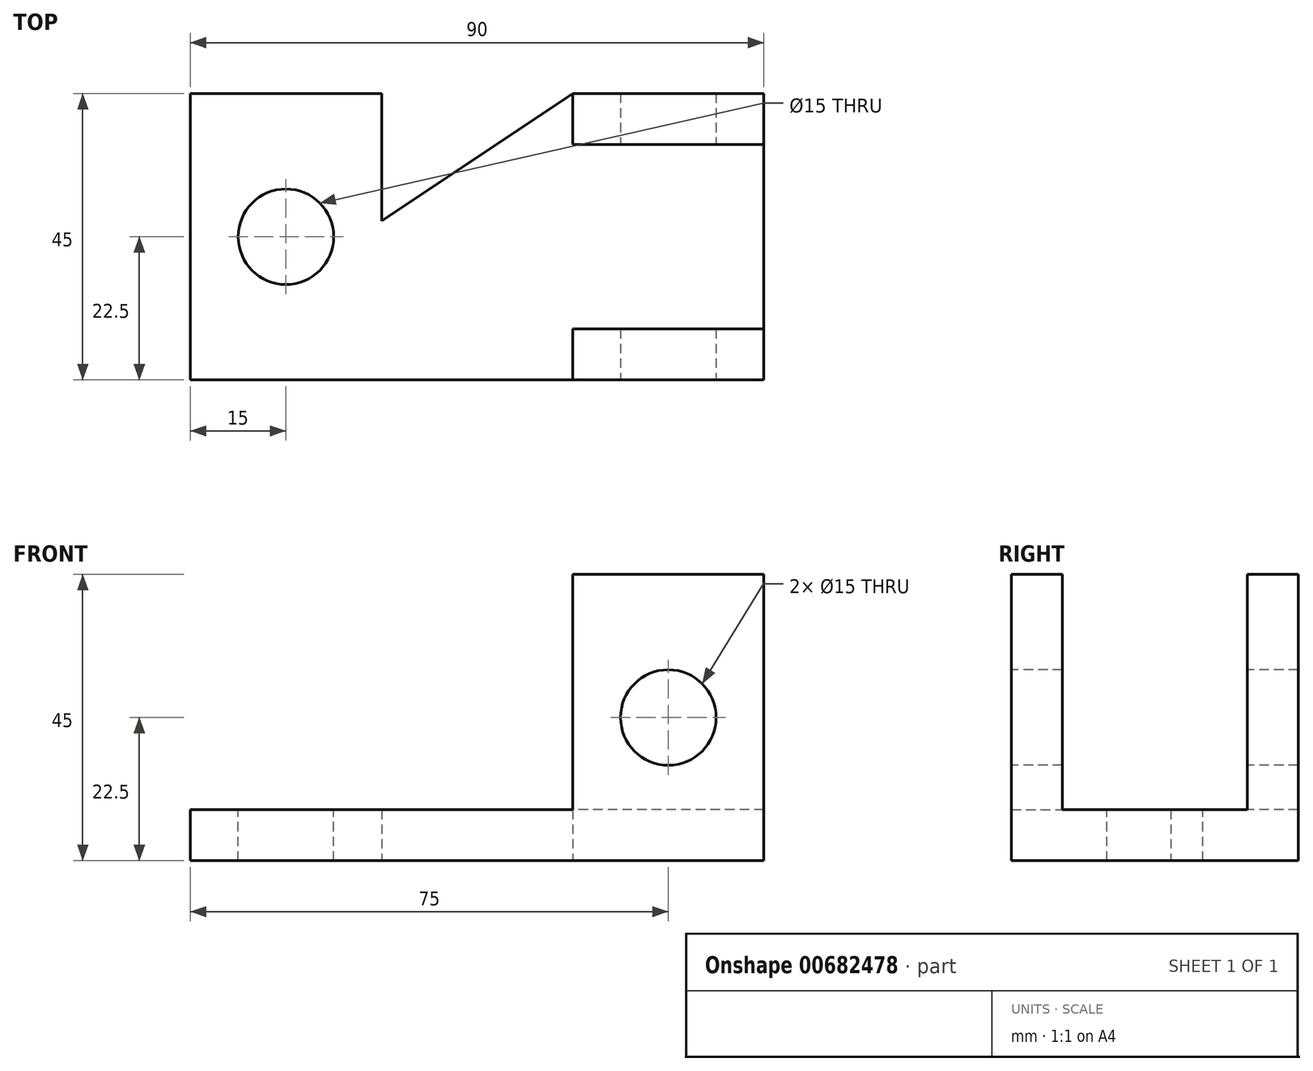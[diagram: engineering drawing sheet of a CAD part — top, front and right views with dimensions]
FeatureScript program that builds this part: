
annotation { "Feature Type Name" : "Feature", "Feature Type Description" : "" }
export const myFeature = defineFeature(function(context is Context, id is Id, definition is map)
    precondition{}
    {
        {
            var Q0;
            Q0=qCreatedBy(makeId("Top.planeOp"),FACE);
            var sketch = newSketch(context, id + "F0", { "sketchPlane" : qUnion([Q0])});
            skLineSegment(sketch, "E0.bottom", {"start": v(0, 0) * mm, "end": v(90, 0) * mm});
            skLineSegment(sketch, "E0.top", {"start": v(0, 45) * mm, "end": v(30, 45) * mm});
            skLineSegment(sketch, "E0.left", {"start": v(0, 0) * mm, "end": v(0, 45) * mm});
            skLineSegment(sketch, "E0.right", {"start": v(90, 0) * mm, "end": v(90, 45) * mm});
            skLineSegment(sketch, "E1", {"start": v(30, 25) * mm, "end": v(30, 45) * mm});
            skLineSegment(sketch, "E2", {"start": v(30, 25) * mm, "end": v(60, 45) * mm});
            skLineSegment(sketch, "E3.trimOffspring", {"start": v(60, 45) * mm, "end": v(90, 45) * mm});
            skSolve(sketch);
        }
        {
            var Q0;
            Q0 = qSketchRegion(id + "F0", true);
            extrude(context, id + "F1", {"entities" : qUnion([Q0]), "depth" : 8 * mm, "offsetDistance" : 25 * mm});
        }
        {
            var Q0;
            Q0=makeQuery(id+"F1.opExtrude","CAP_FACE",FACE,{"disambiguationData":[OSD([sQuery(id+"F0.wireOp",EDGE,"E0.bottom"),sQuery(id+"F0.wireOp",EDGE,"E0.top"),sQuery(id+"F0.wireOp",EDGE,"E0.left"),sQuery(id+"F0.wireOp",EDGE,"E0.right"),sQuery(id+"F0.wireOp",EDGE,"E1"),sQuery(id+"F0.wireOp",EDGE,"E2"),sQuery(id+"F0.wireOp",EDGE,"E3.trimOffspring")])],"isStart":false});
            var sketch = newSketch(context, id + "F2", { "sketchPlane" : qUnion([Q0])});
            skLineSegment(sketch, "E4.bottom", {"start": v(60, 45) * mm, "end": v(90, 45) * mm});
            skLineSegment(sketch, "E4.top", {"start": v(60, 37) * mm, "end": v(90, 37) * mm});
            skLineSegment(sketch, "E4.left", {"start": v(60, 45) * mm, "end": v(60, 37) * mm});
            skLineSegment(sketch, "E4.right", {"start": v(90, 45) * mm, "end": v(90, 37) * mm});
            skLineSegment(sketch, "E5.bottom", {"start": v(90, 0) * mm, "end": v(60, 0) * mm});
            skLineSegment(sketch, "E5.top", {"start": v(90, 8) * mm, "end": v(60, 8) * mm});
            skLineSegment(sketch, "E5.left", {"start": v(90, 0) * mm, "end": v(90, 8) * mm});
            skLineSegment(sketch, "E5.right", {"start": v(60, 0) * mm, "end": v(60, 8) * mm});
            skSolve(sketch);
        }
        {
            var Q0;
            Q0 = qSketchRegion(id + "F2", true);
            extrude(context, id + "F3", {"entities" : qUnion([Q0]), "operationType" : NewBodyOperationType.ADD, "depth" : 37 * mm, "offsetDistance" : 25 * mm});
        }
        {
            var Q0;
            Q0=makeQuery(id+"F3.boolean.opBoolean","MERGE",FACE,{"derivedFrom":[makeQuery(id+"F1.opExtrude","SWEPT_FACE",FACE,{"disambiguationData":[OSD([sQuery(id+"F0.wireOp",EDGE,"E0.bottom")])]}),makeQuery(id+"F3.opExtrude","SWEPT_FACE",FACE,{"disambiguationData":[OSD([sQuery(id+"F2.wireOp",EDGE,"E5.bottom")])]})]});
            var sketch = newSketch(context, id + "F4", { "sketchPlane" : qUnion([Q0])});
            skCircle(sketch, "E6", {"center": v(75, 22.5) * mm, "radius": 7.5 * mm});
            skSolve(sketch);
        }
        {
            var Q0;
            Q0 = qSketchRegion(id + "F4", true);
            extrude(context, id + "F5", {"entities" : qUnion([Q0]), "operationType" : NewBodyOperationType.REMOVE, "endBound" : BoundingType.THROUGH_ALL, "oppositeDirection" : true, "depth" : 25 * mm, "offsetDistance" : 25 * mm});
        }
        {
            var Q0;
            Q0=makeQuery(id+"F1.opExtrude","CAP_FACE",FACE,{"disambiguationData":[OSD([sQuery(id+"F0.wireOp",EDGE,"E0.bottom"),sQuery(id+"F0.wireOp",EDGE,"E0.top"),sQuery(id+"F0.wireOp",EDGE,"E0.left"),sQuery(id+"F0.wireOp",EDGE,"E0.right"),sQuery(id+"F0.wireOp",EDGE,"E1"),sQuery(id+"F0.wireOp",EDGE,"E2"),sQuery(id+"F0.wireOp",EDGE,"E3.trimOffspring")])],"isStart":false});
            var sketch = newSketch(context, id + "F6", { "sketchPlane" : qUnion([Q0])});
            skCircle(sketch, "E7", {"center": v(15, 22.5) * mm, "radius": 7.5 * mm});
            skSolve(sketch);
        }
        {
            var Q0;
            Q0 = qSketchRegion(id + "F6", true);
            extrude(context, id + "F7", {"entities" : qUnion([Q0]), "operationType" : NewBodyOperationType.REMOVE, "oppositeDirection" : true, "depth" : 25 * mm, "offsetDistance" : 25 * mm});
        }
    });
